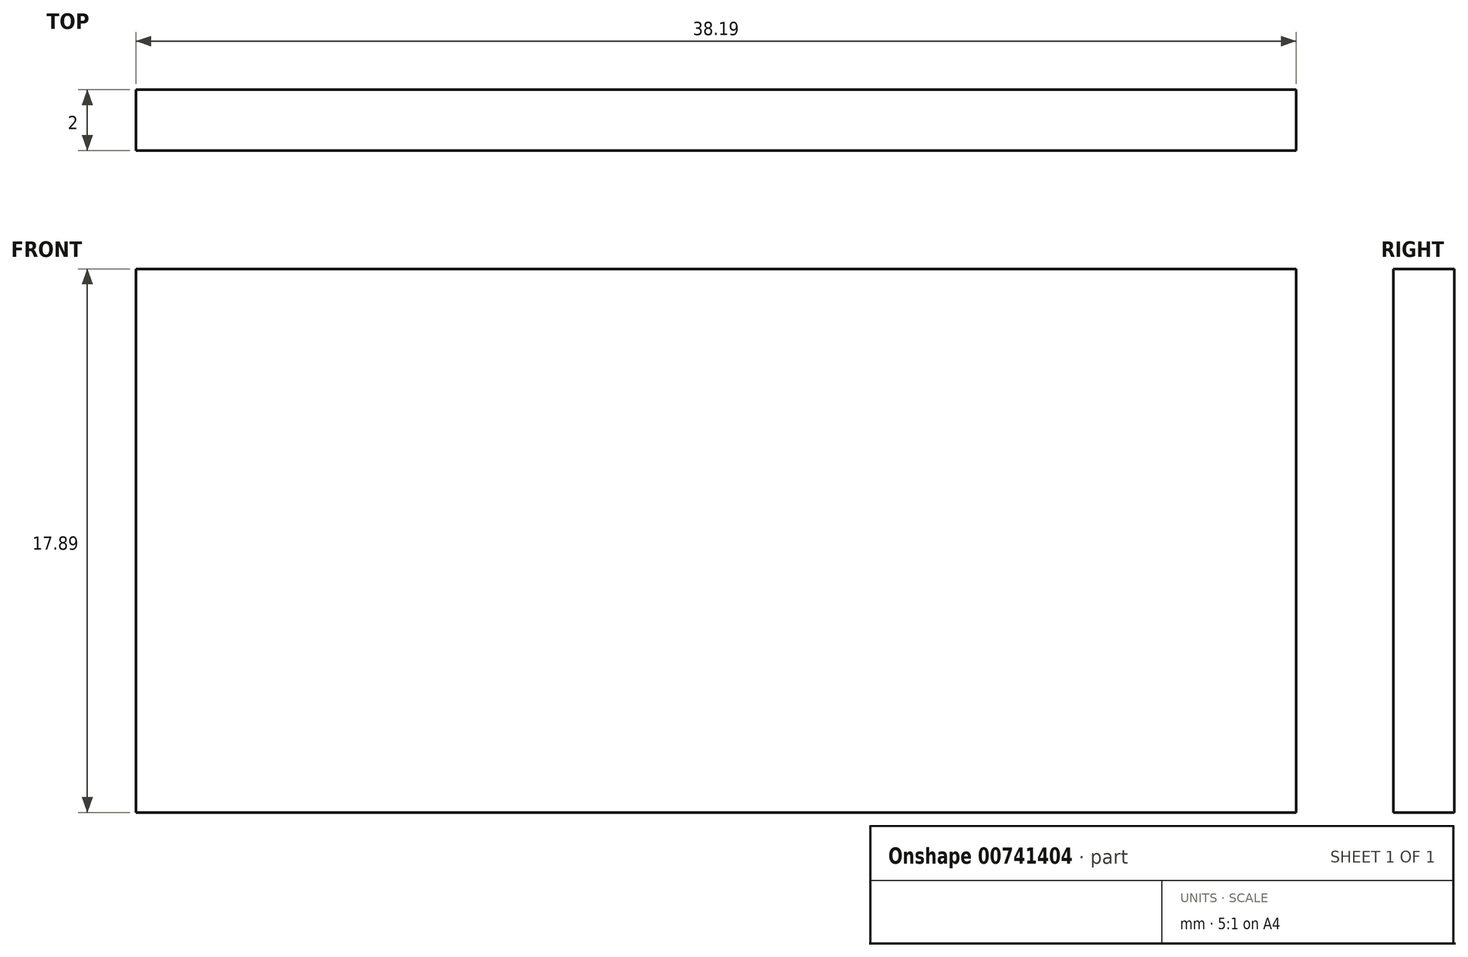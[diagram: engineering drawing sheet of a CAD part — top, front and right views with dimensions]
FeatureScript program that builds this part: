
annotation { "Feature Type Name" : "Feature", "Feature Type Description" : "" }
export const myFeature = defineFeature(function(context is Context, id is Id, definition is map)
    precondition{}
    {
        {
            var Q0;
            Q0=qCreatedBy(makeId("Front.planeOp"),FACE);
            var sketch = newSketch(context, id + "F0", { "sketchPlane" : qUnion([Q0])});
            skLineSegment(sketch, "E0.bottom", {"start": v(-52.14, 28.3) * mm, "end": v(30.25, 28.3) * mm});
            skLineSegment(sketch, "E0.top", {"start": v(-52.14, -13.15) * mm, "end": v(30.25, -13.15) * mm});
            skLineSegment(sketch, "E0.left", {"start": v(-52.14, 28.3) * mm, "end": v(-52.14, -13.15) * mm});
            skLineSegment(sketch, "E0.right", {"start": v(30.25, 28.3) * mm, "end": v(30.25, -13.15) * mm});
            skLineSegment(sketch, "E1.bottom", {"start": v(-63.3, 5.76) * mm, "end": v(-101.49, 5.76) * mm});
            skLineSegment(sketch, "E1.top", {"start": v(-63.3, -12.13) * mm, "end": v(-101.49, -12.13) * mm});
            skLineSegment(sketch, "E1.left", {"start": v(-63.3, 5.76) * mm, "end": v(-63.3, -12.13) * mm});
            skLineSegment(sketch, "E1.right", {"start": v(-101.49, 5.76) * mm, "end": v(-101.49, -12.13) * mm});
            skSolve(sketch);
        }
        {
            var Q0;
            Q0=makeQuery(id+"F0.imprint","IMPRINT",FACE,{"disambiguationData":[TD([[makeQuery(id+"F0.imprint","IMPRINT",EDGE,{"derivedFrom":sQuery(id+"F0.wireOp",EDGE,"E1.bottom")}),1.0]])]});
            extrude(context, id + "F1", {"entities" : qUnion([Q0]), "depth" : 2 * mm, "offsetDistance" : 25.4 * mm});
        }
    });
